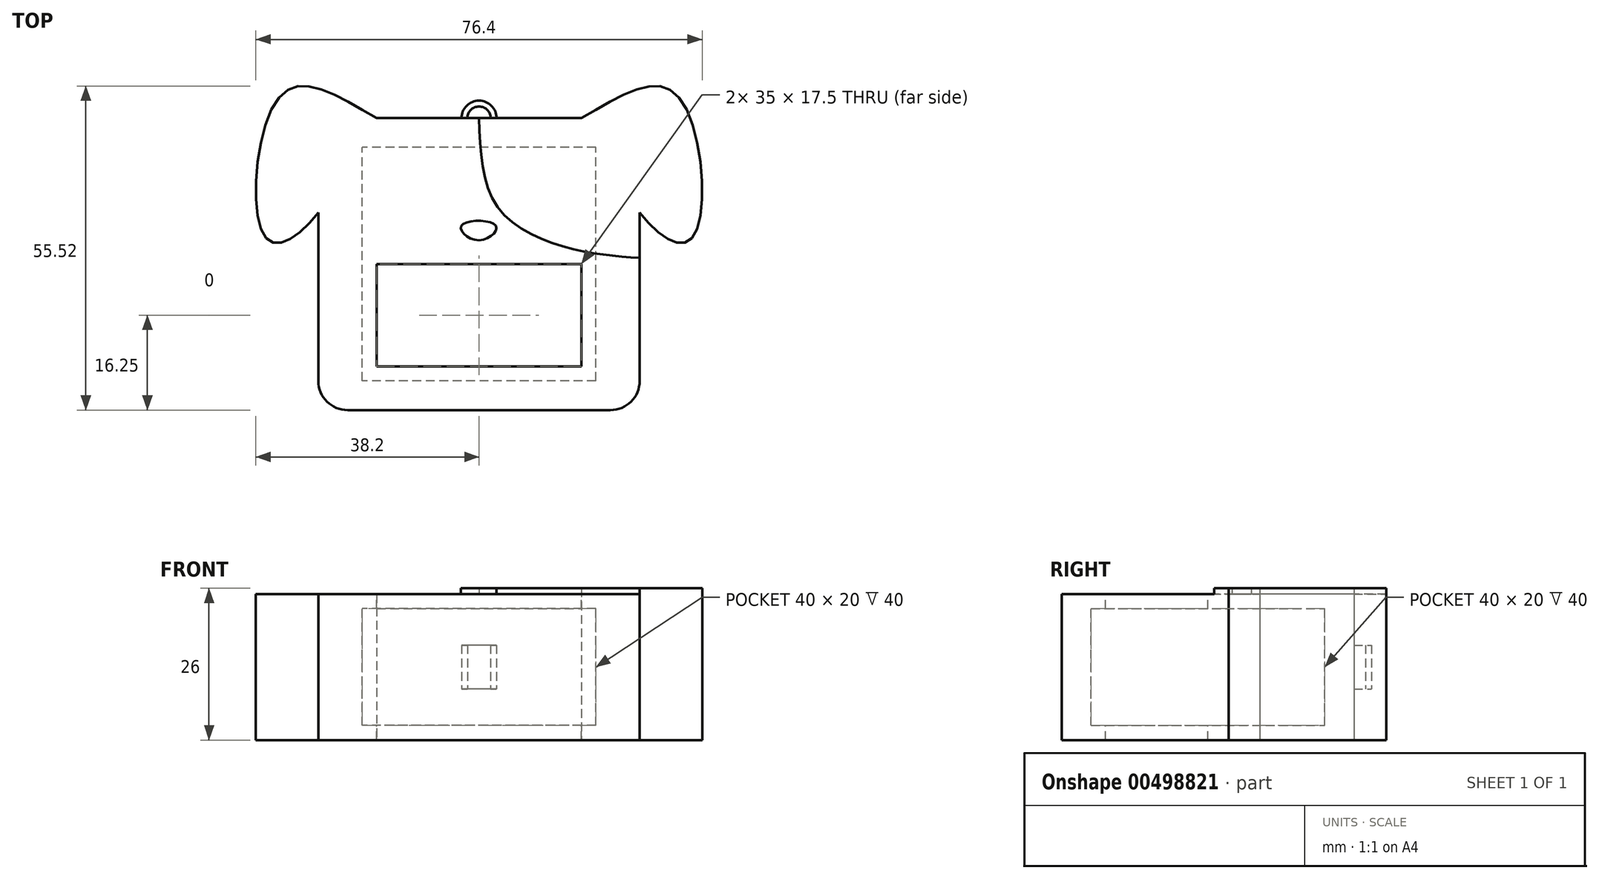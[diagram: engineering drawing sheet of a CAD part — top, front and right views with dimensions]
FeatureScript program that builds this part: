
annotation { "Feature Type Name" : "Feature", "Feature Type Description" : "" }
export const myFeature = defineFeature(function(context is Context, id is Id, definition is map)
    precondition{}
    {
        {
            var Q0;
            Q0=qCreatedBy(makeId("Top.planeOp"),FACE);
            var sketch = newSketch(context, id + "F0", { "sketchPlane" : qUnion([Q0])});
            skLineSegment(sketch, "E0.bottom", {"start": v(20, -20) * mm, "end": v(-20, -20) * mm});
            skLineSegment(sketch, "E0.top", {"start": v(20, 20) * mm, "end": v(-20, 20) * mm});
            skLineSegment(sketch, "E0.left", {"start": v(20, -20) * mm, "end": v(20, 20) * mm});
            skLineSegment(sketch, "E0.right", {"start": v(-20, -20) * mm, "end": v(-20, 20) * mm});
            skPoint(sketch, "E0.middle", {"position": v(0, 0) * mm});
            skSolve(sketch);
        }
        {
            var Q0;
            Q0=qCreatedBy(makeId("Top.planeOp"),FACE);
            var sketch = newSketch(context, id + "F1", { "sketchPlane" : qUnion([Q0])});
            skLineSegment(sketch, "E1.bottom", {"start": v(17.5, -17.5) * mm, "end": v(-17.5, -17.5) * mm});
            skLineSegment(sketch, "E1.left", {"start": v(17.5, -17.5) * mm, "end": v(17.5, 0) * mm});
            skLineSegment(sketch, "E1.right", {"start": v(-17.5, -17.5) * mm, "end": v(-17.5, 0) * mm});
            skPoint(sketch, "E1.middle", {"position": v(0, 0) * mm});
            skLineSegment(sketch, "E2", {"start": v(-17.5, 0) * mm, "end": v(17.5, 0) * mm});
            skPoint(sketch, "E1.top.start.orphan", {"position": v(17.5, 17.5) * mm});
            skPoint(sketch, "E3.orphan", {"position": v(-17.5, 17.5) * mm});
            skSolve(sketch);
        }
        {
            var Q0;
            Q0=qCreatedBy(makeId("Top.planeOp"),FACE);
            var sketch = newSketch(context, id + "F2", { "sketchPlane" : qUnion([Q0])});
            skLineSegment(sketch, "E4.bottom", {"start": v(27.5, -25) * mm, "end": v(-27.5, -25) * mm});
            skLineSegment(sketch, "E4.top", {"start": v(17.5, 25) * mm, "end": v(-17.5, 25) * mm});
            skLineSegment(sketch, "E4.left", {"start": v(27.5, -25) * mm, "end": v(27.5, 8.86) * mm});
            skLineSegment(sketch, "E4.right", {"start": v(-27.5, -25) * mm, "end": v(-27.5, 8.86) * mm});
            skPoint(sketch, "E4.middle", {"position": v(0, 0) * mm});
            skFitSpline(sketch, "E5", {"points": [v(-17.5, 25) * mm, v(-33.83, 29) * mm, v(-36.36, 4.35) * mm, v(-27.5, 8.86) * mm], "startDerivative": vector(-58.33, 32.73) * mm, "endDerivative": vector(34.15, 44.27) * mm});
            skFitSpline(sketch, "E6.MirrorCS", {"points": [v(17.5, 25) * mm, v(33.83, 29) * mm, v(36.36, 4.35) * mm, v(27.5, 8.86) * mm], "startDerivative": vector(58.33, 32.73) * mm, "endDerivative": vector(-34.15, 44.27) * mm});
            skPoint(sketch, "E7.orphan", {"position": v(-27.5, 25) * mm});
            skPoint(sketch, "E8.orphan", {"position": v(27.5, 25) * mm});
            skSolve(sketch);
        }
        {
            var Q0;
            Q0=qSketchRegion(id+"F2",true);
            extrude(context, id + "F3", {"entities" : qUnion([Q0]), "endBound" : BoundingType.SYMMETRIC, "depth" : 25 * mm});
        }
        {
            var Q0;
            Q0=qSketchRegion(id+"F0",true);
            extrude(context, id + "F4", {"entities" : qUnion([Q0]), "operationType" : NewBodyOperationType.REMOVE, "endBound" : BoundingType.SYMMETRIC, "oppositeDirection" : true, "depth" : 20 * mm});
        }
        {
            var Q0;
            Q0=qSketchRegion(id+"F1",true);
            extrude(context, id + "F5", {"entities" : qUnion([Q0]), "operationType" : NewBodyOperationType.REMOVE, "endBound" : BoundingType.SYMMETRIC, "oppositeDirection" : true, "depth" : 25 * mm});
        }
        {
            var Q0;
            Q0=makeQuery(id+"F3.opExtrude","CAP_FACE",FACE,{"disambiguationData":[OSD([sQuery(id+"F2.wireOp",EDGE,"E4.bottom"),sQuery(id+"F2.wireOp",EDGE,"E4.top"),sQuery(id+"F2.wireOp",EDGE,"E4.left"),sQuery(id+"F2.wireOp",EDGE,"E4.right"),sQuery(id+"F2.wireOp",EDGE,"E5"),sQuery(id+"F2.wireOp",EDGE,"E6.MirrorCS")])],"isStart":false});
            var sketch = newSketch(context, id + "F6", { "sketchPlane" : qUnion([Q0])});
            skFitSpline(sketch, "E9", {"points": [v(0, 4.1) * mm, v(2.84, 6.6) * mm, v(-3, 6.6) * mm, v(0, 4.1) * mm]});
            skLineSegment(sketch, "E10", {"start": v(0, 4.1) * mm, "end": v(0, 0) * mm});
            skFitSpline(sketch, "E11", {"points": [v(0, 25) * mm, v(3.38, 9.53) * mm, v(16.34, 2.54) * mm, v(27.5, 1.07) * mm], "startDerivative": vector(1.76, -48.6) * mm, "endDerivative": vector(35.28, -2.44) * mm});
            skSolve(sketch);
        }
        {
            var Q0;
            Q0=qSketchRegion(id+"F6",true);
            var Q1;
            Q1=sQuery(id+"F6.wireOp",EDGE,"E9");
            extrude(context, id + "F7", {"entities" : qUnion([Q0]), "surfaceEntities" : qUnion([Q1]), "depth" : 1 * mm});
        }
        {
            var Q0;
            Q0=qCreatedBy(makeId("Top.planeOp"),FACE);
            var sketch = newSketch(context, id + "F8", { "sketchPlane" : qUnion([Q0])});
            skArc(sketch, "E12", {"start": v(0, 28) * mm, "mid": v(2.12, 27.12) * mm, "end": v(3, 25) * mm});
            skArc(sketch, "E13.MirrorCS", {"start": v(0, 28) * mm, "mid": v(-2.12, 27.12) * mm, "end": v(-3, 25) * mm});
            skArc(sketch, "E14", {"start": v(0, 27) * mm, "mid": v(1.41, 26.41) * mm, "end": v(2, 25) * mm});
            skArc(sketch, "E15.MirrorCS", {"start": v(0, 27) * mm, "mid": v(-1.41, 26.41) * mm, "end": v(-2, 25) * mm});
            skLineSegment(sketch, "E16", {"start": v(-3, 25) * mm, "end": v(-2, 25) * mm});
            skLineSegment(sketch, "E17", {"start": v(2, 25) * mm, "end": v(3, 25) * mm});
            skSolve(sketch);
        }
        {
            var Q0;
            Q0=qSketchRegion(id+"F8",true);
            extrude(context, id + "F9", {"entities" : qUnion([Q0]), "operationType" : NewBodyOperationType.ADD, "endBound" : BoundingType.SYMMETRIC, "depth" : 7.5 * mm});
        }
        {
            var Q0;
            {var subQ0=sQuery(id+"F6.wireOp",EDGE,"E11");Q0=makeQuery(id+"F6.imprint","IMPRINT",FACE,{"disambiguationData":[TD([[makeQuery(id+"F6.imprint","IMPRINT",EDGE,{"derivedFrom":subQ0}),1.0]])]});}
            extrude(context, id + "F10", {"entities" : qUnion([Q0]), "operationType" : NewBodyOperationType.ADD, "depth" : 1 * mm});
        }
        {
            var Q0;
            Q0=makeQuery(id+"F3.opExtrude","SWEPT_EDGE",EDGE,{"disambiguationData":[OSD([sQuery(id+"F2.wireOp",EDGE,"E4.bottom"),sQuery(id+"F2.wireOp",EDGE,"E4.left")])]});
            var Q1;
            Q1=makeQuery(id+"F3.opExtrude","SWEPT_EDGE",EDGE,{"disambiguationData":[OSD([sQuery(id+"F2.wireOp",EDGE,"E4.bottom"),sQuery(id+"F2.wireOp",EDGE,"E4.right")])]});
            fillet(context, id + "F11", {"entities" : qUnion([Q0, Q1]), "radius" : 5 * mm, "tangentPropagation" : true, "allowEdgeOverflow" : false});
        }
    });
